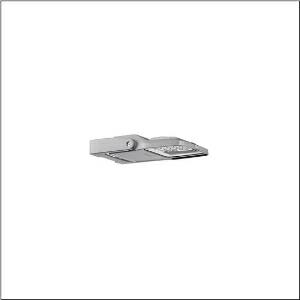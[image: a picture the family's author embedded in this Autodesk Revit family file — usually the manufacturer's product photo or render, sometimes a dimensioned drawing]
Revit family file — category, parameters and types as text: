
# Revit family: floodlight_fl_21_iq_micro___pl64_5xa7761a2e2a_9d46
name_source: partatom
category: Lighting Fixtures
units: mm (PartAtom-declared; Revit-internal decimal feet)

## family parameters
Cut with Voids When Loaded = No
Host = Face
Light Source = No
Part Type = Normal
Room Calculation Point = No
Round Connector Dimension = Use Diameter
Shared = No

## types (1)
- --- (1 x LED, 2870 lm, 23.1 W, 3000K)
    Apparent Load = 23 VA
    CIE Flux Codes = 28 80 98 100 100
    Color Rendering = 70
    Color Temperature = 3000K
    Default Elevation = 1800 mm
    Description = Floodlight FL 21 iQ micro, floodlight, primary light control with lens, of PMMA, primary optical cover: protective disc, of toughened safety glass, transparent, light distribution: PL64, light emission: direct distribution, installation type: surface-mounted, LED, High Power LED, rated luminous flux: 2.870lm, luminous efficacy: 124lm/W, light colour: 730, colour temperature: 3000K, control gear: iQ Comfort/DALI, control: optimised constant luminous flux control (CLO 2.0), Desk-Remote (wireless, voltage-free reading and setting of iQ features in the workshop via application-optimized NFC function/RFID function), Light-Fading, Smart-Wire, Night-Set, Lumen-Switch, Temp-Guard, Auto-Match, with terminal, 6-pole, mains connection: 220..240V, AC, 50/60Hz, start of lifetime: 23W, end of service life: 24W, reduction: 11W, luminaire housing, of diecast aluminium, powder-coated, Siteco® metallic grey (DB 702S), corrosivity category C5 mid according to DIN EN ISO 12944, suitable for swimming pools, chlorine-resistant, sealing non-destructively replaceable, design bracket, of diecast aluminium, powder-coated, Siteco® metallic grey (DB 702S), protection rating (complete): IP66, insulation class (complete): insulation class II (safety insulation), certification: CE, ENEC, VDE, protection symbol: D, impact resistance: IK07, permissible operating ambient temperature: -40..+40°C, permissible operating ambient temperature for outdoor applications: -40..+50°C, standard: DIN EN 12944, LABS conformity tested according to VDMA 24364:2018-05, packaging unit: 1 piece

Light Distribution: PL64
    Height = 65 mm
    Lamp = 1 x LED
    Lamp Light Flux = 2870 lm
    Lamp Power = 23.1 W
    Lamp count = 1
    Length = 312 mm
    Luminous efficacy = 124 lm/W
    Manufacturer = Siteco
    ModVariant = No
    Model = 5XA7761A2E2A
    Mounting Place = Wall
    Mounting Type = Surface mounted
    Number of Poles = 1
    OnlyDefault = Yes
    Power Factor = 1
    Product Name = Floodlight FL 21 iQ micro | PL64
    Product group = floodlight | wall mounted
    ProductGroupID = 2001
    Protection Class = Protection class II
    Protection Degree = IP 66
    RLX_Detail_Level = 1
    RLX_Emergency_Light_Flux = 0 lm
    RLX_Emergency_Type = 0
    RLX_Emergency_Type_DB = No
    RlxData = <blob elided: 97505 chars, md5=33283597>
    Socket = socket
    Standby Power = 0 W
    System Light Flux = 2870 lm
    System Power = 23 W
    Type Comments = factory setting: luminous flux: 100 % | dim-lin: 254 | 455 mA
    Type Image = l_1006878.jpg
    URL = http://relux.com
    VarID = @adj_180866
    Voltage = 0 V
    Weight = 0.00 kg
    Width = 230 mm

## geometry (parser evidence)
native form markers: Blend x4, Sweep x14
no freeform markers — native parametric forms only
